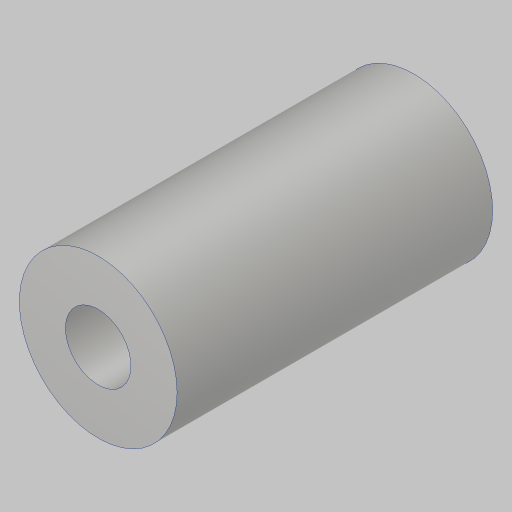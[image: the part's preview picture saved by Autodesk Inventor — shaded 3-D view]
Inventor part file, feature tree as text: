
AUTODESK INVENTOR PART (.ipt)
format: ipt  version: 2023.5 (Build 275446000, 446)  size: 119,296 bytes
history: native  units: in
note: dims shown in document units (in); Inventor stores cm internally (conversion verified against a paired STEP export)
features: extrude x1, hole x1
ambient origin geometry x8: Origin, YZ Plane, XZ Plane, XY Plane, X Axis, Y Axis, Z Axis, Center Point
bodies: Solid1 (feature_tree)
feature tree (2):
  extrude  "Extrusion1"  Depth=0.75in
  hole  "Hole1"  [1 undecoded]
note: 1 required parameter value undecoded (feature->parameter linkage not recoverable at this tier; creation-order binding heuristic only, values carry confidence <= 0.55)
